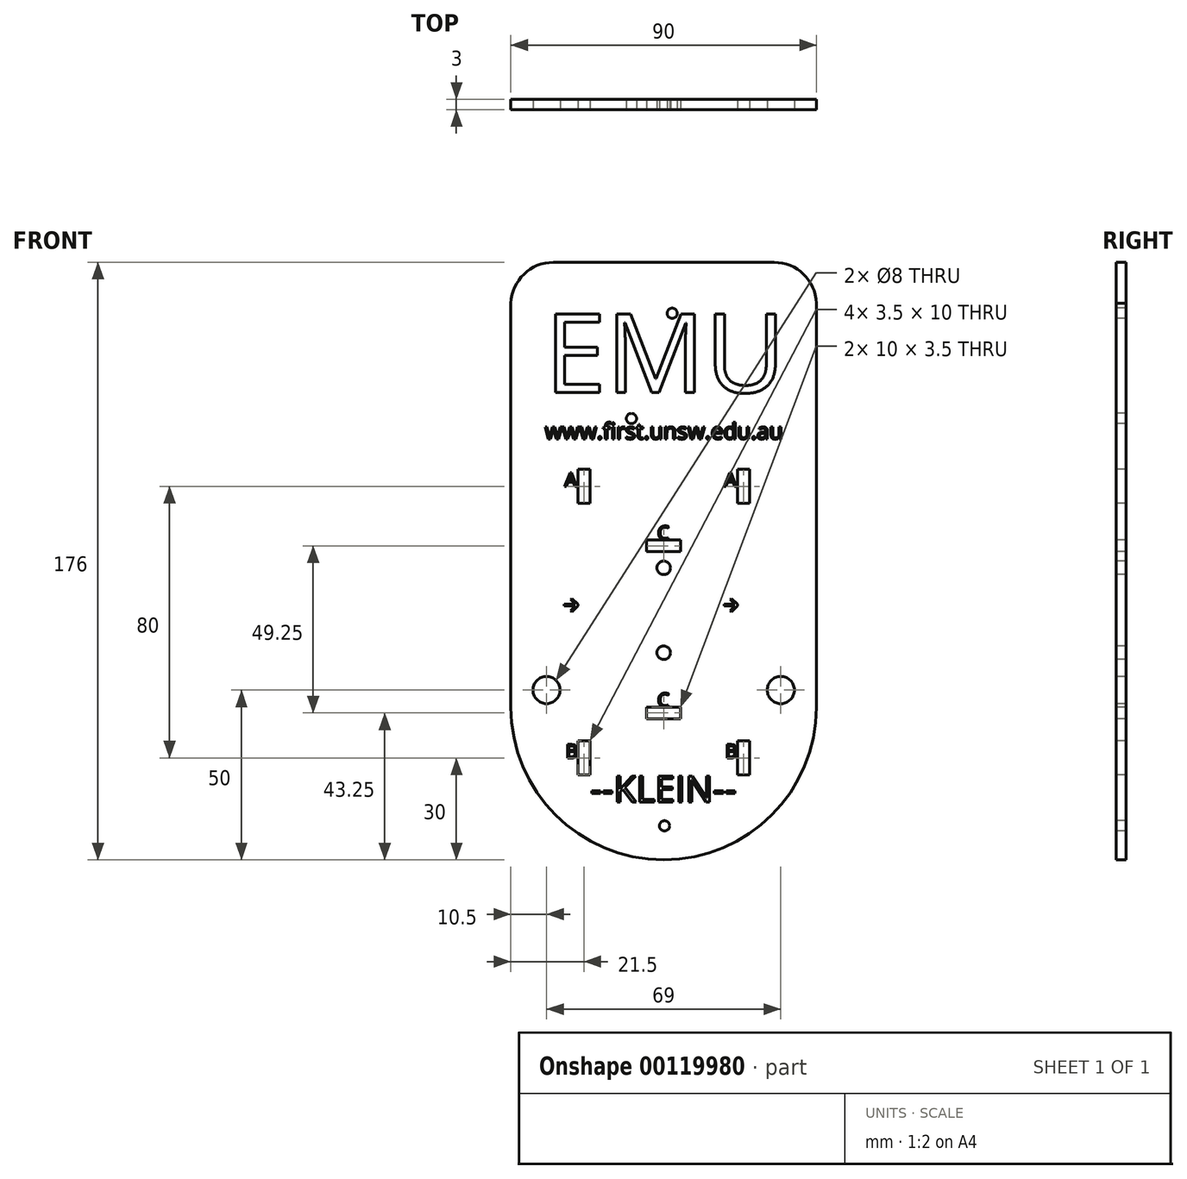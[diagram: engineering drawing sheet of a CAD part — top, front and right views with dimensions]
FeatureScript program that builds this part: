
annotation { "Feature Type Name" : "Feature", "Feature Type Description" : "" }
export const myFeature = defineFeature(function(context is Context, id is Id, definition is map)
    precondition{}
    {
        {
            var Q0;
            Q0=qCreatedBy(makeId("Front.planeOp"),FACE);
            var sketch = newSketch(context, id + "F0", { "sketchPlane" : qUnion([Q0])});
            skLineSegment(sketch, "E0.bottom", {"start": v(0, 0) * mm, "end": v(-90, 0) * mm});
            skLineSegment(sketch, "E0.top", {"start": v(0, 135) * mm, "end": v(-90, 135) * mm});
            skLineSegment(sketch, "E0.left", {"start": v(0, 0) * mm, "end": v(0, 135) * mm});
            skLineSegment(sketch, "E0.right", {"start": v(-90, 0) * mm, "end": v(-90, 135) * mm});
            skArc(sketch, "E1", {"start": v(-90, 0) * mm, "mid": v(-45, -45) * mm, "end": v(0, 0) * mm});
            skSolve(sketch);
        }
        {
            var Q0;
            Q0=makeQuery(id+"F0.imprint","IMPRINT",FACE,{"disambiguationData":[TD([[makeQuery(id+"F0.imprint","IMPRINT",EDGE,{"derivedFrom":sQuery(id+"F0.wireOp",EDGE,"E0.bottom")}),-1.0]])]});
            var Q1;
            Q1=makeQuery(id+"F0.imprint","IMPRINT",FACE,{"disambiguationData":[TD([[makeQuery(id+"F0.imprint","IMPRINT",EDGE,{"derivedFrom":sQuery(id+"F0.wireOp",EDGE,"E0.bottom")}),1.0]])]});
            var Q2;
            {var subQ6=sQuery(id+"F0.wireOp",EDGE,"Co1CvtZ1-7VFD-wMyC-hBqh-fkG4D9t2zfZJ");Q2=makeQuery(id+"F0.imprint","IMPRINT",FACE,{"disambiguationData":[TD([[makeQuery(id+"F0.imprint","IMPRINT",EDGE,{"derivedFrom":subQ6}),1.0]])]});}
            extrude(context, id + "F1", {"entities" : qUnion([Q0, Q1, Q2]), "depth" : 3 * mm});
        }
        {
            var Q0;
            Q0=makeQuery(id+"F1.opExtrude","CAP_FACE",FACE,{"disambiguationData":[OSD([sQuery(id+"F0.wireOp",EDGE,"E0.top"),sQuery(id+"F0.wireOp",EDGE,"E0.left"),sQuery(id+"F0.wireOp",EDGE,"E0.right"),sQuery(id+"F0.wireOp",EDGE,"E1")])],"isStart":false});
            var sketch = newSketch(context, id + "F2", { "sketchPlane" : qUnion([Q0])});
            skLineSegment(sketch, "E2.bottom", {"start": v(-19.75, 70) * mm, "end": v(-23.25, 70) * mm});
            skLineSegment(sketch, "E2.top", {"start": v(-19.75, 60) * mm, "end": v(-23.25, 60) * mm});
            skLineSegment(sketch, "E2.left", {"start": v(-19.75, 70) * mm, "end": v(-19.75, 60) * mm});
            skLineSegment(sketch, "E2.right", {"start": v(-23.25, 70) * mm, "end": v(-23.25, 60) * mm});
            skLineSegment(sketch, "E3.bottom", {"start": v(-70.25, 70) * mm, "end": v(-66.75, 70) * mm});
            skLineSegment(sketch, "E3.top", {"start": v(-70.25, 60) * mm, "end": v(-66.75, 60) * mm});
            skLineSegment(sketch, "E3.left", {"start": v(-70.25, 70) * mm, "end": v(-70.25, 60) * mm});
            skLineSegment(sketch, "E3.right", {"start": v(-66.75, 70) * mm, "end": v(-66.75, 60) * mm});
            skLineSegment(sketch, "E4.bottom", {"start": v(-19.75, -10) * mm, "end": v(-23.25, -10) * mm});
            skLineSegment(sketch, "E4.top", {"start": v(-19.75, -20) * mm, "end": v(-23.25, -20) * mm});
            skLineSegment(sketch, "E4.left", {"start": v(-19.75, -10) * mm, "end": v(-19.75, -20) * mm});
            skLineSegment(sketch, "E4.right", {"start": v(-23.25, -10) * mm, "end": v(-23.25, -20) * mm});
            skLineSegment(sketch, "E5.bottom", {"start": v(-70.25, -10) * mm, "end": v(-66.75, -10) * mm});
            skLineSegment(sketch, "E5.top", {"start": v(-70.25, -20) * mm, "end": v(-66.75, -20) * mm});
            skLineSegment(sketch, "E5.left", {"start": v(-70.25, -10) * mm, "end": v(-70.25, -20) * mm});
            skLineSegment(sketch, "E5.right", {"start": v(-66.75, -10) * mm, "end": v(-66.75, -20) * mm});
            skLineSegment(sketch, "E6.bottom", {"start": v(-40, 49.25) * mm, "end": v(-50, 49.25) * mm});
            skLineSegment(sketch, "E6.top", {"start": v(-40, 45.75) * mm, "end": v(-50, 45.75) * mm});
            skLineSegment(sketch, "E6.left", {"start": v(-40, 49.25) * mm, "end": v(-40, 45.75) * mm});
            skLineSegment(sketch, "E6.right", {"start": v(-50, 49.25) * mm, "end": v(-50, 45.75) * mm});
            skLineSegment(sketch, "E7.bottom", {"start": v(-40, 0) * mm, "end": v(-50, 0) * mm});
            skLineSegment(sketch, "E7.top", {"start": v(-40, -3.5) * mm, "end": v(-50, -3.5) * mm});
            skLineSegment(sketch, "E7.left", {"start": v(-40, 0) * mm, "end": v(-40, -3.5) * mm});
            skLineSegment(sketch, "E7.right", {"start": v(-50, 0) * mm, "end": v(-50, -3.5) * mm});
            skSolve(sketch);
        }
        {
            var Q0;
            Q0=makeQuery(id+"F2.imprint","IMPRINT",FACE,{"disambiguationData":[TD([[makeQuery(id+"F2.imprint","IMPRINT",EDGE,{"derivedFrom":sQuery(id+"F2.wireOp",EDGE,"E6.bottom")}),1.0]])]});
            var Q1;
            Q1=makeQuery(id+"F2.imprint","IMPRINT",FACE,{"disambiguationData":[TD([[makeQuery(id+"F2.imprint","IMPRINT",EDGE,{"derivedFrom":sQuery(id+"F2.wireOp",EDGE,"E2.bottom")}),1.0]])]});
            var Q2;
            Q2=makeQuery(id+"F2.imprint","IMPRINT",FACE,{"disambiguationData":[TD([[makeQuery(id+"F2.imprint","IMPRINT",EDGE,{"derivedFrom":sQuery(id+"F2.wireOp",EDGE,"E3.bottom")}),-1.0]])]});
            var Q3;
            Q3=makeQuery(id+"F2.imprint","IMPRINT",FACE,{"disambiguationData":[TD([[makeQuery(id+"F2.imprint","IMPRINT",EDGE,{"derivedFrom":sQuery(id+"F2.wireOp",EDGE,"E7.bottom")}),1.0]])]});
            var Q4;
            Q4=makeQuery(id+"F2.imprint","IMPRINT",FACE,{"disambiguationData":[TD([[makeQuery(id+"F2.imprint","IMPRINT",EDGE,{"derivedFrom":sQuery(id+"F2.wireOp",EDGE,"E5.bottom")}),-1.0]])]});
            var Q5;
            Q5=makeQuery(id+"F2.imprint","IMPRINT",FACE,{"disambiguationData":[TD([[makeQuery(id+"F2.imprint","IMPRINT",EDGE,{"derivedFrom":sQuery(id+"F2.wireOp",EDGE,"E4.bottom")}),1.0]])]});
            extrude(context, id + "F3", {"entities" : qUnion([Q0, Q1, Q2, Q3, Q4, Q5]), "operationType" : NewBodyOperationType.REMOVE, "oppositeDirection" : true, "depth" : 25 * mm});
        }
        {
            var Q0;
            Q0=makeQuery(id+"F1.opExtrude","CAP_FACE",FACE,{"disambiguationData":[OSD([sQuery(id+"F0.wireOp",EDGE,"E0.top"),sQuery(id+"F0.wireOp",EDGE,"E0.left"),sQuery(id+"F0.wireOp",EDGE,"E0.right"),sQuery(id+"F0.wireOp",EDGE,"E1")])],"isStart":false});
            var sketch = newSketch(context, id + "F4", { "sketchPlane" : qUnion([Q0])});
            skCircle(sketch, "E8", {"center": v(-10.5, 5) * mm, "radius": 4 * mm});
            skCircle(sketch, "E9", {"center": v(-79.5, 5) * mm, "radius": 4 * mm});
            skLineSegment(sketch, "E10", {"start": v(-79.5, 15) * mm, "end": v(-79.5, -0.98) * mm, "construction": true});
            skPoint(sketch, "E10.endSnap0", {"position": v(-79.5, 15) * mm});
            skLineSegment(sketch, "E11", {"start": v(-10.5, 15) * mm, "end": v(-10.5, -2.12) * mm, "construction": true});
            skSolve(sketch);
        }
        {
            var Q0;
            Q0=makeQuery(id+"F4.imprint","IMPRINT",FACE,{"disambiguationData":[TD([[makeQuery(id+"F4.imprint","IMPRINT",EDGE,{"derivedFrom":sQuery(id+"F4.wireOp",EDGE,"E8")}),1.0]])]});
            var Q1;
            Q1=makeQuery(id+"F4.imprint","IMPRINT",FACE,{"disambiguationData":[TD([[makeQuery(id+"F4.imprint","IMPRINT",EDGE,{"derivedFrom":sQuery(id+"F4.wireOp",EDGE,"E9")}),1.0]])]});
            extrude(context, id + "F5", {"entities" : qUnion([Q0, Q1]), "operationType" : NewBodyOperationType.REMOVE, "oppositeDirection" : true, "depth" : 25 * mm});
        }
        {
            var Q0;
            Q0=makeQuery(id+"F1.opExtrude","CAP_FACE",FACE,{"disambiguationData":[OSD([sQuery(id+"F0.wireOp",EDGE,"E0.top"),sQuery(id+"F0.wireOp",EDGE,"E0.left"),sQuery(id+"F0.wireOp",EDGE,"E0.right"),sQuery(id+"F0.wireOp",EDGE,"E1")])],"isStart":false});
            var sketch = newSketch(context, id + "F6", { "sketchPlane" : qUnion([Q0])});
            skCircle(sketch, "E12", {"center": v(-44.75, -35) * mm, "radius": 1.5 * mm});
            skPoint(sketch, "E12.centerSnap0", {"position": v(-44.75, -35) * mm});
            skCircle(sketch, "E13", {"center": v(-37.75, -35) * mm, "radius": 1.5 * mm});
            skLineSegment(sketch, "E14", {"start": v(0, 118) * mm, "end": v(-90, 118) * mm});
            skLineSegment(sketch, "E15", {"start": v(-12.5, 131) * mm, "end": v(-77.5, 131) * mm});
            skArc(sketch, "E16", {"start": v(0, 118) * mm, "mid": v(-3.48, 127.16) * mm, "end": v(-12.5, 131) * mm});
            skArc(sketch, "E17", {"start": v(-77.5, 131) * mm, "mid": v(-86.52, 127.16) * mm, "end": v(-90, 118) * mm});
            skSolve(sketch);
        }
        {
            var Q0;
            Q0=makeQuery(id+"F6.imprint","IMPRINT",FACE,{"disambiguationData":[TD([[makeQuery(id+"F6.imprint","IMPRINT",EDGE,{"derivedFrom":sQuery(id+"F6.wireOp",EDGE,"E12")}),1.0]])]});
            var Q1;
            {var subQ1=sQuery(id+"F6.wireOp",EDGE,"E15");Q1=makeQuery(id+"F6.imprint","IMPRINT",FACE,{"disambiguationData":[TD([[makeQuery(id+"F6.imprint","IMPRINT",EDGE,{"derivedFrom":subQ1}),-1.0]])]});}
            extrude(context, id + "F7", {"entities" : qUnion([Q0, Q1]), "operationType" : NewBodyOperationType.REMOVE, "oppositeDirection" : true, "depth" : 25 * mm});
        }
        {
            var Q0;
            Q0=makeQuery(id+"F1.opExtrude","CAP_FACE",FACE,{"disambiguationData":[OSD([sQuery(id+"F0.wireOp",EDGE,"E0.top"),sQuery(id+"F0.wireOp",EDGE,"E0.left"),sQuery(id+"F0.wireOp",EDGE,"E0.right"),sQuery(id+"F0.wireOp",EDGE,"E1")])],"isStart":false});
            var sketch = newSketch(context, id + "F8", { "sketchPlane" : qUnion([Q0])});
            skLineSegment(sketch, "E18.bottom", {"start": v(-51.25, -28.5) * mm, "end": v(-37.25, -28.5) * mm, "construction": true});
            skLineSegment(sketch, "E18.top", {"start": v(-51.25, -59.5) * mm, "end": v(-37.25, -59.5) * mm, "construction": true});
            skLineSegment(sketch, "E18.left", {"start": v(-51.25, -28.5) * mm, "end": v(-51.25, -59.5) * mm, "construction": true});
            skLineSegment(sketch, "E18.right", {"start": v(-37.25, -28.5) * mm, "end": v(-37.25, -59.5) * mm, "construction": true});
            skLineSegment(sketch, "E19.bottom", {"start": v(-75, -4) * mm, "end": v(-15, -4) * mm, "construction": true});
            skLineSegment(sketch, "E19.top", {"start": v(-75, 61) * mm, "end": v(-15, 61) * mm, "construction": true});
            skLineSegment(sketch, "E19.left", {"start": v(-75, -4) * mm, "end": v(-75, 61) * mm, "construction": true});
            skLineSegment(sketch, "E19.right", {"start": v(-15, -4) * mm, "end": v(-15, 61) * mm, "construction": true});
            skLineSegment(sketch, "E20.bottom", {"start": v(-66.5, 131) * mm, "end": v(-23.5, 131) * mm, "construction": true});
            skLineSegment(sketch, "E20.top", {"start": v(-66.5, 73) * mm, "end": v(-23.5, 73) * mm, "construction": true});
            skLineSegment(sketch, "E20.left", {"start": v(-66.5, 131) * mm, "end": v(-66.5, 73) * mm, "construction": true});
            skLineSegment(sketch, "E20.right", {"start": v(-23.5, 131) * mm, "end": v(-23.5, 73) * mm, "construction": true});
            skLineSegment(sketch, "E21", {"start": v(-45, 131) * mm, "end": v(-45, -4) * mm, "construction": true});
            skPoint(sketch, "E21.endSnap0", {"position": v(-45, -4) * mm});
            skCircle(sketch, "E22", {"center": v(-54.5, 85) * mm, "radius": 1.5 * mm});
            skCircle(sketch, "E23", {"center": v(-42.5, 116) * mm, "radius": 1.5 * mm});
            skCircle(sketch, "E24", {"center": v(-45, 41) * mm, "radius": 2 * mm});
            skCircle(sketch, "E25", {"center": v(-45, 16) * mm, "radius": 2 * mm});
            skSolve(sketch);
        }
        {
            var Q0;
            Q0=makeQuery(id+"F8.imprint","IMPRINT",FACE,{"disambiguationData":[TD([[makeQuery(id+"F8.imprint","IMPRINT",EDGE,{"derivedFrom":sQuery(id+"F8.wireOp",EDGE,"vshc7AOB-qd1c-EgLO-rvy1-nh1xwlupcqY1")}),1.0]])]});
            var Q1;
            Q1=makeQuery(id+"F8.imprint","IMPRINT",FACE,{"disambiguationData":[TD([[makeQuery(id+"F8.imprint","IMPRINT",EDGE,{"derivedFrom":sQuery(id+"F8.wireOp",EDGE,"ahrcOYQZ-7xab-KB6G-vDZ9-1v2IvBEjBigj")}),1.0]])]});
            var Q2;
            Q2=makeQuery(id+"F8.imprint","IMPRINT",FACE,{"disambiguationData":[TD([[makeQuery(id+"F8.imprint","IMPRINT",EDGE,{"derivedFrom":sQuery(id+"F8.wireOp",EDGE,"E22")}),1.0]])]});
            var Q3;
            Q3=makeQuery(id+"F8.imprint","IMPRINT",FACE,{"disambiguationData":[TD([[makeQuery(id+"F8.imprint","IMPRINT",EDGE,{"derivedFrom":sQuery(id+"F8.wireOp",EDGE,"E23")}),1.0]])]});
            var Q4;
            Q4=makeQuery(id+"F8.imprint","IMPRINT",FACE,{"disambiguationData":[TD([[makeQuery(id+"F8.imprint","IMPRINT",EDGE,{"derivedFrom":sQuery(id+"F8.wireOp",EDGE,"E24")}),1.0]])]});
            var Q5;
            Q5=makeQuery(id+"F8.imprint","IMPRINT",FACE,{"disambiguationData":[TD([[makeQuery(id+"F8.imprint","IMPRINT",EDGE,{"derivedFrom":sQuery(id+"F8.wireOp",EDGE,"E25")}),1.0]])]});
            extrude(context, id + "F9", {"entities" : qUnion([Q0, Q1, Q2, Q3, Q4, Q5]), "operationType" : NewBodyOperationType.REMOVE, "oppositeDirection" : true, "depth" : 25 * mm});
        }
        {
            var Q0;
            Q0=makeQuery(id+"F1.opExtrude","CAP_FACE",FACE,{"disambiguationData":[OSD([sQuery(id+"F0.wireOp",EDGE,"E0.top"),sQuery(id+"F0.wireOp",EDGE,"E0.left"),sQuery(id+"F0.wireOp",EDGE,"E0.right"),sQuery(id+"F0.wireOp",EDGE,"E1")])],"isStart":false});
            var sketch = newSketch(context, id + "F10", { "sketchPlane" : qUnion([Q0])});
            skText(sketch, "E26", { "text": "A", "fontName": "OpenSans-Regular.ttf"});
            skLineSegment(sketch, "E27", {"start": v(-27.13, 67) * mm, "end": v(-23.25, 67) * mm, "construction": true});
            skText(sketch, "E28", { "text": "B", "fontName": "OpenSans-Regular.ttf"});
            skLineSegment(sketch, "E29", {"start": v(-26.9, -13) * mm, "end": v(-23.25, -13) * mm, "construction": true});
            skLineSegment(sketch, "E30", {"start": v(-45, 0) * mm, "end": v(-45, 45.75) * mm, "construction": true});
            skText(sketch, "E31", { "text": "B", "fontName": "OpenSans-Regular.ttf"});
            skLineSegment(sketch, "E32", {"start": v(-73.9, -13) * mm, "end": v(-70.25, -13) * mm, "construction": true});
            skText(sketch, "E33", { "text": "A", "fontName": "OpenSans-Regular.ttf"});
            skLineSegment(sketch, "E34", {"start": v(-74.13, 67) * mm, "end": v(-70.25, 67) * mm, "construction": true});
            skText(sketch, "E35", { "text": "C", "fontName": "OpenSans-Regular.ttf"});
            skText(sketch, "E36", { "text": "C", "fontName": "OpenSans-Regular.ttf"});
            skText(sketch, "E37", { "text": "EMU", "fontName": "OpenSans-Regular.ttf"});
            skText(sketch, "E38", { "text": "www.first.unsw.edu.au", "fontName": "OpenSans-Regular.ttf"});
            skLineSegment(sketch, "E39", {"start": v(-70.25, -10) * mm, "end": v(-70.25, 60) * mm, "construction": true});
            skLineSegment(sketch, "E40", {"start": v(-23.25, 60) * mm, "end": v(-23.25, -10) * mm, "construction": true});
            skLineSegment(sketch, "E41.bottom", {"start": v(-70.25, 28) * mm, "end": v(-74.25, 28) * mm, "construction": true});
            skLineSegment(sketch, "E41.top", {"start": v(-70.25, 32) * mm, "end": v(-74.25, 32) * mm, "construction": true});
            skLineSegment(sketch, "E41.left", {"start": v(-70.25, 28) * mm, "end": v(-70.25, 32) * mm, "construction": true});
            skLineSegment(sketch, "E41.right", {"start": v(-74.25, 28) * mm, "end": v(-74.25, 32) * mm, "construction": true});
            skLineSegment(sketch, "E42.bottom", {"start": v(-23.25, 28) * mm, "end": v(-27.25, 28) * mm, "construction": true});
            skLineSegment(sketch, "E42.top", {"start": v(-23.25, 32) * mm, "end": v(-27.25, 32) * mm, "construction": true});
            skLineSegment(sketch, "E42.left", {"start": v(-23.25, 28) * mm, "end": v(-23.25, 32) * mm});
            skLineSegment(sketch, "E42.right", {"start": v(-27.25, 28) * mm, "end": v(-27.25, 32) * mm, "construction": true});
            skLineSegment(sketch, "E43", {"start": v(-74.25, 30) * mm, "end": v(-70.25, 30) * mm, "construction": true});
            skLineSegment(sketch, "E44", {"start": v(-27.25, 30) * mm, "end": v(-23.25, 30) * mm, "construction": true});
            skLineSegment(sketch, "E45.bottom", {"start": v(-74.25, 29.75) * mm, "end": v(-70.96, 29.75) * mm});
            skLineSegment(sketch, "E45.top", {"start": v(-74.25, 30.25) * mm, "end": v(-70.96, 30.25) * mm});
            skLineSegment(sketch, "E45.left", {"start": v(-74.25, 29.75) * mm, "end": v(-74.25, 30.25) * mm});
            skLineSegment(sketch, "E45.right", {"start": v(-70.25, 29.75) * mm, "end": v(-70.25, 30.25) * mm});
            skLineSegment(sketch, "E46", {"start": v(-70.25, 29.75) * mm, "end": v(-72, 28) * mm});
            skLineSegment(sketch, "E47", {"start": v(-72, 28) * mm, "end": v(-72.35, 28.35) * mm});
            skLineSegment(sketch, "E48", {"start": v(-72.35, 28.35) * mm, "end": v(-70.96, 29.75) * mm});
            skLineSegment(sketch, "E49", {"start": v(-70.25, 30.25) * mm, "end": v(-72, 32) * mm});
            skLineSegment(sketch, "E50", {"start": v(-72, 32) * mm, "end": v(-72.35, 31.65) * mm});
            skLineSegment(sketch, "E51", {"start": v(-72.35, 31.65) * mm, "end": v(-70.96, 30.25) * mm});
            skLineSegment(sketch, "E52.bottom", {"start": v(-27.25, 29.75) * mm, "end": v(-23.96, 29.75) * mm});
            skLineSegment(sketch, "E52.top", {"start": v(-27.25, 30.25) * mm, "end": v(-23.96, 30.25) * mm});
            skLineSegment(sketch, "E52.left", {"start": v(-27.25, 29.75) * mm, "end": v(-27.25, 30.25) * mm});
            skLineSegment(sketch, "E52.right", {"start": v(-23.25, 29.75) * mm, "end": v(-23.25, 30.25) * mm});
            skLineSegment(sketch, "E53", {"start": v(-23.25, 30.25) * mm, "end": v(-25, 32) * mm});
            skLineSegment(sketch, "E54", {"start": v(-25, 32) * mm, "end": v(-25.35, 31.65) * mm});
            skLineSegment(sketch, "E55", {"start": v(-25.35, 31.65) * mm, "end": v(-23.96, 30.25) * mm});
            skLineSegment(sketch, "E56", {"start": v(-23.25, 29.75) * mm, "end": v(-25, 28) * mm});
            skLineSegment(sketch, "E57", {"start": v(-25, 28) * mm, "end": v(-25.35, 28.35) * mm});
            skLineSegment(sketch, "E58", {"start": v(-25.35, 28.35) * mm, "end": v(-23.96, 29.75) * mm});
            skText(sketch, "E59", { "text": "--KLEIN--", "fontName": "OpenSans-Regular.ttf"});
            const initialGuessF10  = {"E26": [-0.02713, 0.065, 1, 0, 0.004], "E28": [-0.0269, -0.015, 1, 0, 0.004], "E31": [-0.0739, -0.015, 1, 0, 0.004], "E33": [-0.07413, 0.065, 1, 0, 0.004], "E35": [-0.04685, 0.0001, 1, 0, 0.004], "E36": [-0.04685, 0.04935, 1, 0, 0.004], "E37": [-0.08, 0.09268, 1, 0, 0.02332], "E38": [-0.08, 0.07894, 1, 0, 0.00473], "E59": [-0.06667, -0.02799, 1, 0, 0.00774]};
            skSetInitialGuess(sketch, initialGuessF10);
            skSolve(sketch);
        }
        {
            var Q0;
            Q0=makeQuery(id+"F10.imprint","IMPRINT",FACE,{"disambiguationData":[TD([[makeQuery(id+"F10.imprint","IMPRINT",EDGE,{"derivedFrom":sQuery(id+"F10.wireOp",EDGE,"E35.sketch_text.stroke-0")}),-1.0]])]});
            var Q1;
            Q1=makeQuery(id+"F10.imprint","IMPRINT",FACE,{"disambiguationData":[TD([[makeQuery(id+"F10.imprint","IMPRINT",EDGE,{"derivedFrom":sQuery(id+"F10.wireOp",EDGE,"E31.sketch_text.stroke-0")}),-1.0]])]});
            var Q2;
            Q2=makeQuery(id+"F10.imprint","IMPRINT",FACE,{"disambiguationData":[TD([[makeQuery(id+"F10.imprint","IMPRINT",EDGE,{"derivedFrom":sQuery(id+"F10.wireOp",EDGE,"E28.sketch_text.stroke-0")}),-1.0]])]});
            var Q3;
            Q3=makeQuery(id+"F10.imprint","IMPRINT",FACE,{"disambiguationData":[TD([[makeQuery(id+"F10.imprint","IMPRINT",EDGE,{"derivedFrom":sQuery(id+"F10.wireOp",EDGE,"E36.sketch_text.stroke-0")}),-1.0]])]});
            var Q4;
            Q4=makeQuery(id+"F10.imprint","IMPRINT",FACE,{"disambiguationData":[TD([[makeQuery(id+"F10.imprint","IMPRINT",EDGE,{"derivedFrom":sQuery(id+"F10.wireOp",EDGE,"E26.sketch_text.stroke-0")}),-1.0]])]});
            var Q5;
            Q5=makeQuery(id+"F10.imprint","IMPRINT",FACE,{"disambiguationData":[TD([[makeQuery(id+"F10.imprint","IMPRINT",EDGE,{"derivedFrom":sQuery(id+"F10.wireOp",EDGE,"E33.sketch_text.stroke-0")}),-1.0]])]});
            var Q6;
            Q6=makeQuery(id+"F10.imprint","IMPRINT",FACE,{"disambiguationData":[TD([[makeQuery(id+"F10.imprint","IMPRINT",EDGE,{"derivedFrom":sQuery(id+"F10.wireOp",EDGE,"E38.sketch_text.stroke-0")}),-1.0]])]});
            var Q7;
            Q7=makeQuery(id+"F10.imprint","IMPRINT",FACE,{"disambiguationData":[TD([[makeQuery(id+"F10.imprint","IMPRINT",EDGE,{"derivedFrom":sQuery(id+"F10.wireOp",EDGE,"E38.sketch_text.stroke-23")}),-1.0]])]});
            var Q8;
            Q8=makeQuery(id+"F10.imprint","IMPRINT",FACE,{"disambiguationData":[TD([[makeQuery(id+"F10.imprint","IMPRINT",EDGE,{"derivedFrom":sQuery(id+"F10.wireOp",EDGE,"E38.sketch_text.stroke-46")}),-1.0]])]});
            var Q9;
            Q9=makeQuery(id+"F10.imprint","IMPRINT",FACE,{"disambiguationData":[TD([[makeQuery(id+"F10.imprint","IMPRINT",EDGE,{"derivedFrom":sQuery(id+"F10.wireOp",EDGE,"E38.sketch_text.stroke-69")}),-1.0]])]});
            var Q10;
            Q10=makeQuery(id+"F10.imprint","IMPRINT",FACE,{"disambiguationData":[TD([[makeQuery(id+"F10.imprint","IMPRINT",EDGE,{"derivedFrom":sQuery(id+"F10.wireOp",EDGE,"E38.sketch_text.stroke-77")}),-1.0]])]});
            var Q11;
            Q11=makeQuery(id+"F10.imprint","IMPRINT",FACE,{"disambiguationData":[TD([[makeQuery(id+"F10.imprint","IMPRINT",EDGE,{"derivedFrom":sQuery(id+"F10.wireOp",EDGE,"E38.sketch_text.stroke-94")}),-1.0]])]});
            var Q12;
            Q12=makeQuery(id+"F10.imprint","IMPRINT",FACE,{"disambiguationData":[TD([[makeQuery(id+"F10.imprint","IMPRINT",EDGE,{"derivedFrom":sQuery(id+"F10.wireOp",EDGE,"E38.sketch_text.stroke-98")}),-1.0]])]});
            var Q13;
            Q13=makeQuery(id+"F10.imprint","IMPRINT",FACE,{"disambiguationData":[TD([[makeQuery(id+"F10.imprint","IMPRINT",EDGE,{"derivedFrom":sQuery(id+"F10.wireOp",EDGE,"E38.sketch_text.stroke-106")}),-1.0]])]});
            var Q14;
            Q14=makeQuery(id+"F10.imprint","IMPRINT",FACE,{"disambiguationData":[TD([[makeQuery(id+"F10.imprint","IMPRINT",EDGE,{"derivedFrom":sQuery(id+"F10.wireOp",EDGE,"E38.sketch_text.stroke-119")}),-1.0]])]});
            var Q15;
            Q15=makeQuery(id+"F10.imprint","IMPRINT",FACE,{"disambiguationData":[TD([[makeQuery(id+"F10.imprint","IMPRINT",EDGE,{"derivedFrom":sQuery(id+"F10.wireOp",EDGE,"E38.sketch_text.stroke-144")}),-1.0]])]});
            var Q16;
            Q16=makeQuery(id+"F10.imprint","IMPRINT",FACE,{"disambiguationData":[TD([[makeQuery(id+"F10.imprint","IMPRINT",EDGE,{"derivedFrom":sQuery(id+"F10.wireOp",EDGE,"E38.sketch_text.stroke-163")}),-1.0]])]});
            var Q17;
            Q17=makeQuery(id+"F10.imprint","IMPRINT",FACE,{"disambiguationData":[TD([[makeQuery(id+"F10.imprint","IMPRINT",EDGE,{"derivedFrom":sQuery(id+"F10.wireOp",EDGE,"E38.sketch_text.stroke-171")}),-1.0]])]});
            var Q18;
            Q18=makeQuery(id+"F10.imprint","IMPRINT",FACE,{"disambiguationData":[TD([[makeQuery(id+"F10.imprint","IMPRINT",EDGE,{"derivedFrom":sQuery(id+"F10.wireOp",EDGE,"E38.sketch_text.stroke-188")}),-1.0]])]});
            var Q19;
            Q19=makeQuery(id+"F10.imprint","IMPRINT",FACE,{"disambiguationData":[TD([[makeQuery(id+"F10.imprint","IMPRINT",EDGE,{"derivedFrom":sQuery(id+"F10.wireOp",EDGE,"E38.sketch_text.stroke-205")}),-1.0]])]});
            var Q20;
            Q20=makeQuery(id+"F10.imprint","IMPRINT",FACE,{"disambiguationData":[TD([[makeQuery(id+"F10.imprint","IMPRINT",EDGE,{"derivedFrom":sQuery(id+"F10.wireOp",EDGE,"E38.sketch_text.stroke-230")}),-1.0]])]});
            var Q21;
            Q21=makeQuery(id+"F10.imprint","IMPRINT",FACE,{"disambiguationData":[TD([[makeQuery(id+"F10.imprint","IMPRINT",EDGE,{"derivedFrom":sQuery(id+"F10.wireOp",EDGE,"E38.sketch_text.stroke-253")}),-1.0]])]});
            var Q22;
            Q22=makeQuery(id+"F10.imprint","IMPRINT",FACE,{"disambiguationData":[TD([[makeQuery(id+"F10.imprint","IMPRINT",EDGE,{"derivedFrom":sQuery(id+"F10.wireOp",EDGE,"E38.sketch_text.stroke-261")}),-1.0]])]});
            var Q23;
            Q23=makeQuery(id+"F10.imprint","IMPRINT",FACE,{"disambiguationData":[TD([[makeQuery(id+"F10.imprint","IMPRINT",EDGE,{"derivedFrom":sQuery(id+"F10.wireOp",EDGE,"E38.sketch_text.stroke-280")}),-1.0]])]});
            var Q24;
            Q24=makeQuery(id+"F10.imprint","IMPRINT",FACE,{"disambiguationData":[TD([[makeQuery(id+"F10.imprint","IMPRINT",EDGE,{"derivedFrom":sQuery(id+"F10.wireOp",EDGE,"E38.sketch_text.stroke-304")}),-1.0]])]});
            var Q25;
            Q25=makeQuery(id+"F10.imprint","IMPRINT",FACE,{"disambiguationData":[TD([[makeQuery(id+"F10.imprint","IMPRINT",EDGE,{"derivedFrom":sQuery(id+"F10.wireOp",EDGE,"E38.sketch_text.stroke-321")}),-1.0]])]});
            var Q26;
            Q26=makeQuery(id+"F10.imprint","IMPRINT",FACE,{"disambiguationData":[TD([[makeQuery(id+"F10.imprint","IMPRINT",EDGE,{"derivedFrom":sQuery(id+"F10.wireOp",EDGE,"E38.sketch_text.stroke-329")}),-1.0]])]});
            var Q27;
            Q27=makeQuery(id+"F10.imprint","IMPRINT",FACE,{"disambiguationData":[TD([[makeQuery(id+"F10.imprint","IMPRINT",EDGE,{"derivedFrom":sQuery(id+"F10.wireOp",EDGE,"E38.sketch_text.stroke-356")}),-1.0]])]});
            var Q28;
            Q28=makeQuery(id+"F10.imprint","IMPRINT",FACE,{"disambiguationData":[TD([[makeQuery(id+"F10.imprint","IMPRINT",EDGE,{"derivedFrom":sQuery(id+"F10.wireOp",EDGE,"E37.sketch_text.stroke-30")}),-1.0]])]});
            var Q29;
            Q29=makeQuery(id+"F10.imprint","IMPRINT",FACE,{"disambiguationData":[TD([[makeQuery(id+"F10.imprint","IMPRINT",EDGE,{"derivedFrom":sQuery(id+"F10.wireOp",EDGE,"E37.sketch_text.stroke-12")}),-1.0]])]});
            var Q30;
            Q30=makeQuery(id+"F10.imprint","IMPRINT",FACE,{"disambiguationData":[TD([[makeQuery(id+"F10.imprint","IMPRINT",EDGE,{"derivedFrom":sQuery(id+"F10.wireOp",EDGE,"E37.sketch_text.stroke-0")}),-1.0]])]});
            var Q31;
            Q31=makeQuery(id+"F10.imprint","IMPRINT",FACE,{"disambiguationData":[TD([[makeQuery(id+"F10.imprint","IMPRINT",EDGE,{"derivedFrom":sQuery(id+"F10.wireOp",EDGE,"E52.bottom")}),1.0]])]});
            var Q32;
            Q32=makeQuery(id+"F10.imprint","IMPRINT",FACE,{"disambiguationData":[TD([[makeQuery(id+"F10.imprint","IMPRINT",EDGE,{"derivedFrom":sQuery(id+"F10.wireOp",EDGE,"E45.bottom")}),1.0]])]});
            var Q33;
            Q33=makeQuery(id+"F10.imprint","IMPRINT",FACE,{"disambiguationData":[TD([[makeQuery(id+"F10.imprint","IMPRINT",EDGE,{"derivedFrom":sQuery(id+"F10.wireOp",EDGE,"E59.sketch_text.stroke-0")}),-1.0]])]});
            var Q34;
            Q34=makeQuery(id+"F10.imprint","IMPRINT",FACE,{"disambiguationData":[TD([[makeQuery(id+"F10.imprint","IMPRINT",EDGE,{"derivedFrom":sQuery(id+"F10.wireOp",EDGE,"E59.sketch_text.stroke-4")}),-1.0]])]});
            var Q35;
            Q35=makeQuery(id+"F10.imprint","IMPRINT",FACE,{"disambiguationData":[TD([[makeQuery(id+"F10.imprint","IMPRINT",EDGE,{"derivedFrom":sQuery(id+"F10.wireOp",EDGE,"E59.sketch_text.stroke-8")}),-1.0]])]});
            var Q36;
            Q36=makeQuery(id+"F10.imprint","IMPRINT",FACE,{"disambiguationData":[TD([[makeQuery(id+"F10.imprint","IMPRINT",EDGE,{"derivedFrom":sQuery(id+"F10.wireOp",EDGE,"E59.sketch_text.stroke-20")}),-1.0]])]});
            var Q37;
            Q37=makeQuery(id+"F10.imprint","IMPRINT",FACE,{"disambiguationData":[TD([[makeQuery(id+"F10.imprint","IMPRINT",EDGE,{"derivedFrom":sQuery(id+"F10.wireOp",EDGE,"E59.sketch_text.stroke-26")}),-1.0]])]});
            var Q38;
            Q38=makeQuery(id+"F10.imprint","IMPRINT",FACE,{"disambiguationData":[TD([[makeQuery(id+"F10.imprint","IMPRINT",EDGE,{"derivedFrom":sQuery(id+"F10.wireOp",EDGE,"E59.sketch_text.stroke-38")}),-1.0]])]});
            var Q39;
            Q39=makeQuery(id+"F10.imprint","IMPRINT",FACE,{"disambiguationData":[TD([[makeQuery(id+"F10.imprint","IMPRINT",EDGE,{"derivedFrom":sQuery(id+"F10.wireOp",EDGE,"E59.sketch_text.stroke-42")}),-1.0]])]});
            var Q40;
            Q40=makeQuery(id+"F10.imprint","IMPRINT",FACE,{"disambiguationData":[TD([[makeQuery(id+"F10.imprint","IMPRINT",EDGE,{"derivedFrom":sQuery(id+"F10.wireOp",EDGE,"E59.sketch_text.stroke-57")}),-1.0]])]});
            var Q41;
            Q41=makeQuery(id+"F10.imprint","IMPRINT",FACE,{"disambiguationData":[TD([[makeQuery(id+"F10.imprint","IMPRINT",EDGE,{"derivedFrom":sQuery(id+"F10.wireOp",EDGE,"E59.sketch_text.stroke-61")}),-1.0]])]});
            extrude(context, id + "F11", {"entities" : qUnion([Q0, Q1, Q2, Q3, Q4, Q5, Q6, Q7, Q8, Q9, Q10, Q11, Q12, Q13, Q14, Q15, Q16, Q17, Q18, Q19, Q20, Q21, Q22, Q23, Q24, Q25, Q26, Q27, Q28, Q29, Q30, Q31, Q32, Q33, Q34, Q35, Q36, Q37, Q38, Q39, Q40, Q41]), "operationType" : NewBodyOperationType.ADD, "depth" : 0 * mm, "offsetDistance" : 25 * mm});
        }
    });
